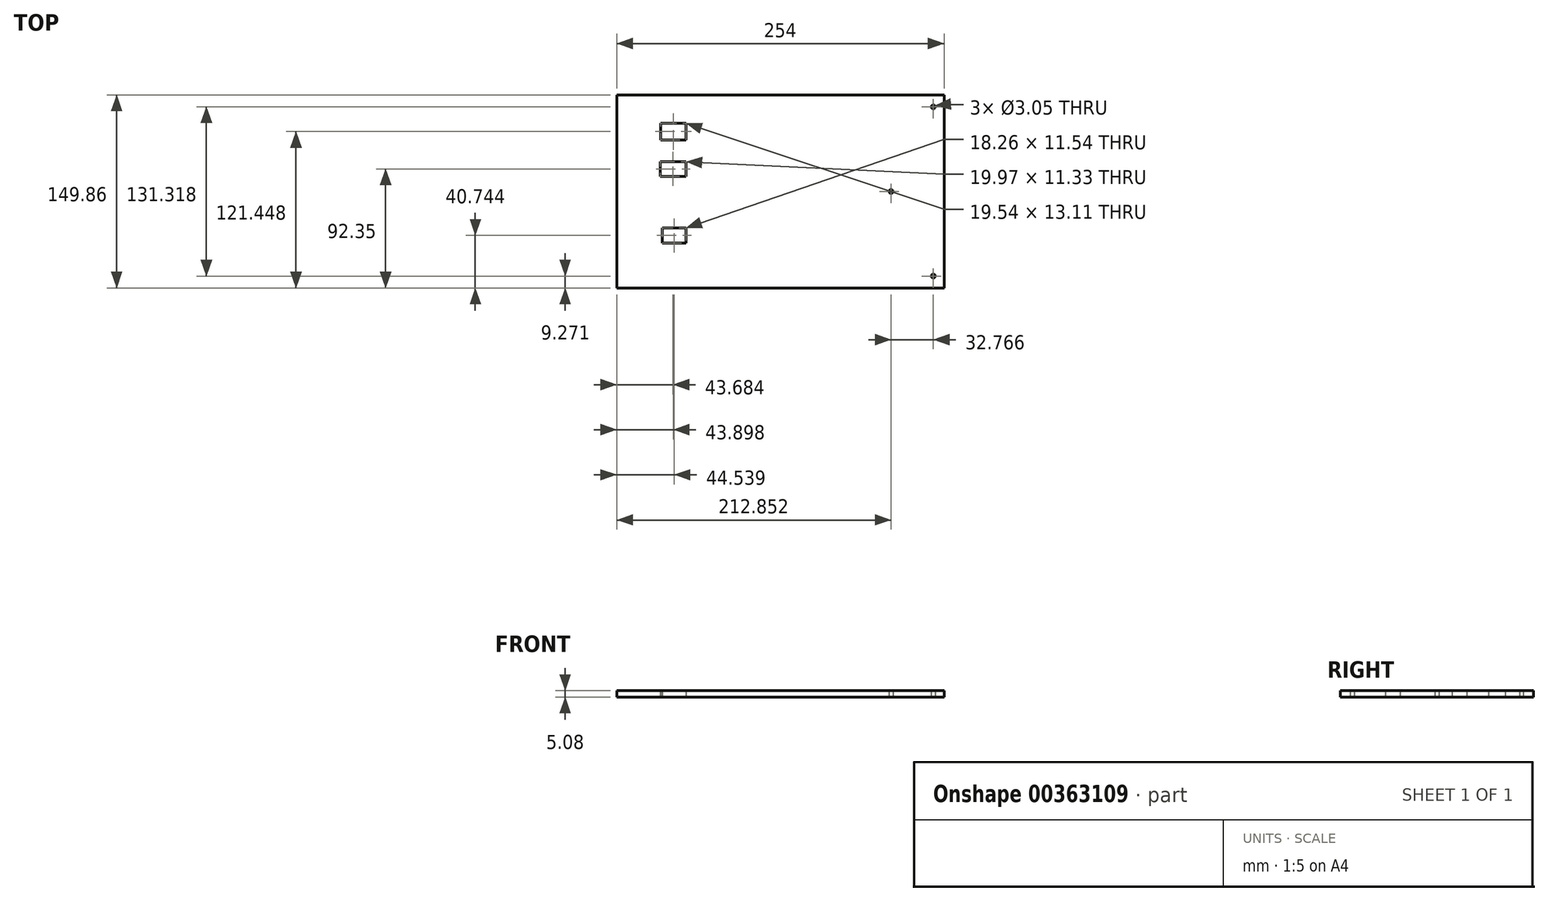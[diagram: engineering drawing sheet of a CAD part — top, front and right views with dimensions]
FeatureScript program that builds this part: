
annotation { "Feature Type Name" : "Feature", "Feature Type Description" : "" }
export const myFeature = defineFeature(function(context is Context, id is Id, definition is map)
    precondition{}
    {
        {
            var Q0;
            Q0=qCreatedBy(makeId("Top.planeOp"),FACE);
            var sketch = newSketch(context, id + "F0", { "sketchPlane" : qUnion([Q0])});
            skLineSegment(sketch, "E0.bottom", {"start": v(0, 0) * mm, "end": v(254, 0) * mm});
            skLineSegment(sketch, "E0.top", {"start": v(0, -149.86) * mm, "end": v(254, -149.86) * mm});
            skLineSegment(sketch, "E0.left", {"start": v(0, 0) * mm, "end": v(0, -149.86) * mm});
            skLineSegment(sketch, "E0.right", {"start": v(254, 0) * mm, "end": v(254, -149.86) * mm});
            skCircle(sketch, "E1", {"center": v(245.62, -9.27) * mm, "radius": 1.52 * mm});
            skCircle(sketch, "E2", {"center": v(212.85, -74.93) * mm, "radius": 1.52 * mm});
            skCircle(sketch, "E3", {"center": v(245.62, -140.59) * mm, "radius": 1.52 * mm});
            skLineSegment(sketch, "E4", {"start": v(245.62, -9.27) * mm, "end": v(245.62, -140.59) * mm, "construction": true});
            skLineSegment(sketch, "E5", {"start": v(245.62, -140.59) * mm, "end": v(245.62, -149.86) * mm, "construction": true});
            skLineSegment(sketch, "E6", {"start": v(245.62, -9.27) * mm, "end": v(245.62, 0) * mm, "construction": true});
            skLineSegment(sketch, "E7", {"start": v(212.85, -74.93) * mm, "end": v(245.62, -74.93) * mm, "construction": true});
            skLineSegment(sketch, "E8", {"start": v(53.67, -15.6) * mm, "end": v(53.67, -133.42) * mm, "construction": true});
            skLineSegment(sketch, "E9.bottom", {"start": v(34.13, -21.86) * mm, "end": v(53.67, -21.86) * mm});
            skLineSegment(sketch, "E9.top", {"start": v(34.13, -34.97) * mm, "end": v(53.67, -34.97) * mm});
            skLineSegment(sketch, "E9.left", {"start": v(34.13, -21.86) * mm, "end": v(34.13, -34.97) * mm});
            skLineSegment(sketch, "E9.right", {"start": v(53.67, -21.86) * mm, "end": v(53.67, -34.97) * mm});
            skLineSegment(sketch, "E10.bottom", {"start": v(33.7, -51.85) * mm, "end": v(53.67, -51.85) * mm});
            skLineSegment(sketch, "E10.top", {"start": v(33.7, -63.17) * mm, "end": v(53.67, -63.17) * mm});
            skLineSegment(sketch, "E10.left", {"start": v(33.7, -51.85) * mm, "end": v(33.7, -63.17) * mm});
            skLineSegment(sketch, "E10.right", {"start": v(53.67, -51.85) * mm, "end": v(53.67, -63.17) * mm});
            skLineSegment(sketch, "E11.bottom", {"start": v(35.4, -103.35) * mm, "end": v(53.67, -103.35) * mm});
            skLineSegment(sketch, "E11.top", {"start": v(35.4, -114.89) * mm, "end": v(53.67, -114.89) * mm});
            skLineSegment(sketch, "E11.left", {"start": v(35.4, -103.35) * mm, "end": v(35.4, -114.89) * mm});
            skLineSegment(sketch, "E11.right", {"start": v(53.67, -103.35) * mm, "end": v(53.67, -114.89) * mm});
            skSolve(sketch);
        }
        {
            var Q0;
            Q0=makeQuery(id+"F0.imprint","IMPRINT",FACE,{"disambiguationData":[TD([[makeQuery(id+"F0.imprint","IMPRINT",EDGE,{"derivedFrom":sQuery(id+"F0.wireOp",EDGE,"E0.bottom")}),-1.0]])]});
            extrude(context, id + "F1", {"entities" : qUnion([Q0]), "depth" : 5.08 * mm});
        }
    });
